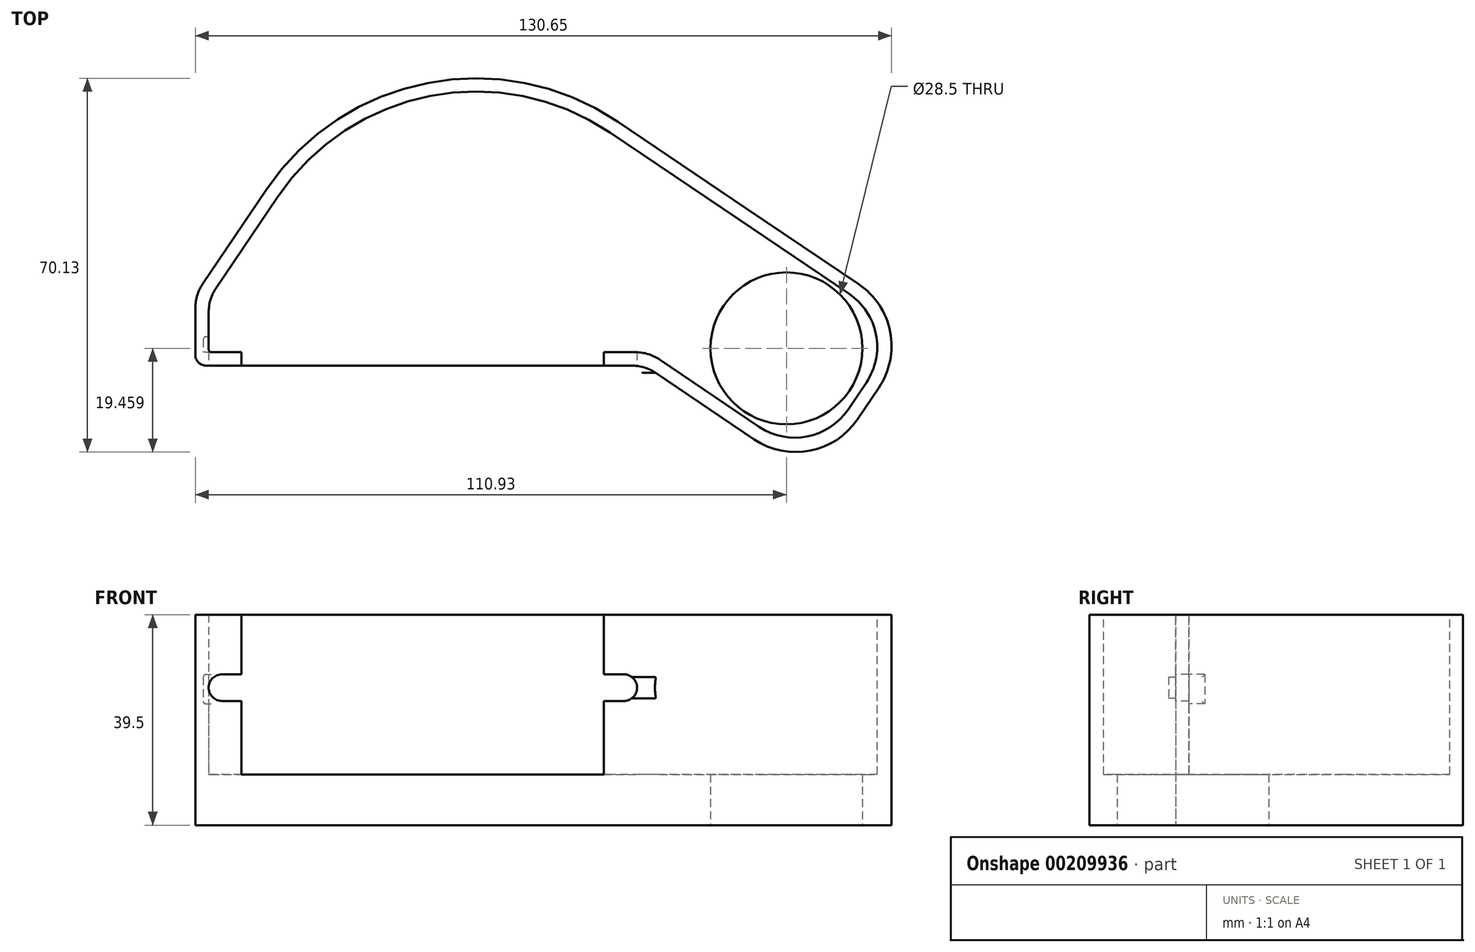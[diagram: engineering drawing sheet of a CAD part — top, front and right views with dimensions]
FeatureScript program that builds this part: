
annotation { "Feature Type Name" : "Feature", "Feature Type Description" : "" }
export const myFeature = defineFeature(function(context is Context, id is Id, definition is map)
    precondition{}
    {
        {
            var Q0;
            Q0=qCreatedBy(makeId("Top.planeOp"),FACE);
            var sketch = newSketch(context, id + "F0", { "sketchPlane" : qUnion([Q0])});
            skLineSegment(sketch, "E0", {"start": v(-46.29, -24.6) * mm, "end": v(36.31, -24.6) * mm});
            skLineSegment(sketch, "E1", {"start": v(-46.29, -24.6) * mm, "end": v(-46.29, -14.6) * mm});
            skLineSegment(sketch, "E2", {"start": v(36.31, -24.6) * mm, "end": v(53.15, 0.36) * mm});
            skLineSegment(sketch, "E3", {"start": v(53.15, 0.36) * mm, "end": v(-8.26, 41.78) * mm});
            skLineSegment(sketch, "E4", {"start": v(-8.26, 41.78) * mm, "end": v(-46.29, -14.6) * mm});
            skLineSegment(sketch, "E5", {"start": v(36.31, -24.6) * mm, "end": v(66.99, -45.29) * mm});
            skLineSegment(sketch, "E6", {"start": v(66.99, -45.29) * mm, "end": v(83.82, -20.33) * mm});
            skLineSegment(sketch, "E7", {"start": v(83.82, -20.33) * mm, "end": v(53.15, 0.36) * mm});
            skCircle(sketch, "E8", {"center": v(62.14, -23.86) * mm, "radius": 14.25 * mm});
            skSolve(sketch);
        }
        {
            var Q0;
            Q0 = qSketchRegion(id + "F0", true);
            extrude(context, id + "F1", {"entities" : qUnion([Q0]), "depth" : 9.15 * mm});
        }
        {
            var Q0;
            Q0=makeQuery(id+"F1.opExtrude","CAP_FACE",FACE,{"disambiguationData":[OSD([sQuery(id+"F0.wireOp",EDGE,"E0"),sQuery(id+"F0.wireOp",EDGE,"E1"),sQuery(id+"F0.wireOp",EDGE,"E2"),sQuery(id+"F0.wireOp",EDGE,"E3"),sQuery(id+"F0.wireOp",EDGE,"E4")])],"isStart":false});
            extrude(context, id + "F2", {"entities" : qUnion([Q0]), "operationType" : NewBodyOperationType.ADD, "depth" : 27.85 * mm});
        }
        {
            var Q0;
            Q0=makeQuery(id+"F2.opExtrude","CAP_FACE",FACE,{"disambiguationData":[OSD([sQuery(id+"F0.wireOp",EDGE,"E0"),sQuery(id+"F0.wireOp",EDGE,"E1"),sQuery(id+"F0.wireOp",EDGE,"E2"),sQuery(id+"F0.wireOp",EDGE,"E3"),sQuery(id+"F0.wireOp",EDGE,"E4")])],"isStart":false});
            var Q1;
            {var subQ0=sQuery(id+"F0.wireOp",EDGE,"E8");Q1=makeQuery(id+"F2.boolean.opBoolean","MERGE",FACE,{"derivedFrom":[makeQuery(id+"F1.opExtrude","SWEPT_FACE",FACE,{"disambiguationData":[OSD([subQ0])]}),makeQuery(id+"F2.opExtrude","SWEPT_FACE",FACE,{"disambiguationData":[OSD([subQ0])]})]});}
            shell(context, id + "F3", {"entities" : qUnion([Q0, Q1]), "thickness" : 2.5 * mm, "oppositeDirection" : true});
        }
        {
            var Q0;
            Q0=makeQuery(id+"F3.opShell","OFFSET_EDGE",EDGE,{"disambiguationData":[OSD([sQuery(id+"F0.wireOp",EDGE,"E3"),sQuery(id+"F0.wireOp",EDGE,"E4")])]});
            fillet(context, id + "F4", {"entities" : qUnion([Q0]), "radius" : 45 * mm, "tangentPropagation" : true, "allowEdgeOverflow" : false});
        }
        {
            var Q0;
            {var subQ0=sQuery(id+"F0.wireOp",EDGE,"E0");var subQ1=makeQuery(id+"F2.boolean.opBoolean","MERGE",FACE,{"derivedFrom":[makeQuery(id+"F1.opExtrude","SWEPT_FACE",FACE,{"disambiguationData":[OSD([subQ0])]}),makeQuery(id+"F2.opExtrude","SWEPT_FACE",FACE,{"disambiguationData":[OSD([subQ0])]})]});Q0=makeQuery(id+"FA12zDWdJS2ZKyh_1.boolean.opBoolean","MERGE",FACE,{"derivedFrom":[makeQuery(id+"FA8GY0G3jhh9Sxv_1.opShell","OFFSET_FACE",FACE,{"disambiguationData":[OSD([subQ0]),TDD([subQ1])]}),subQ1,makeQuery(id+"FA12zDWdJS2ZKyh_1.opExtrude","CAP_FACE",FACE,{"disambiguationData":[OSD([subQ0])],"isStart":false})]});}
            var sketch = newSketch(context, id + "F5", { "sketchPlane" : qUnion([Q0])});
            skCircle(sketch, "E9", {"center": v(-43.79, 23.3) * mm, "radius": 2.5 * mm});
            skCircle(sketch, "E10", {"center": v(31.61, 23.3) * mm, "radius": 2.5 * mm});
            skLineSegment(sketch, "E11", {"start": v(-43.79, 25.8) * mm, "end": v(-40.14, 25.8) * mm});
            skLineSegment(sketch, "E12", {"start": v(-43.79, 20.8) * mm, "end": v(-40.14, 20.8) * mm});
            skLineSegment(sketch, "E13", {"start": v(-40.14, 25.8) * mm, "end": v(-40.14, 37) * mm});
            skLineSegment(sketch, "E14", {"start": v(-40.14, 37) * mm, "end": v(27.86, 37) * mm});
            skLineSegment(sketch, "E15", {"start": v(-40.14, 20.8) * mm, "end": v(-40.14, 0) * mm});
            skLineSegment(sketch, "E16", {"start": v(27.86, 37) * mm, "end": v(27.86, 0) * mm});
            skPoint(sketch, "E16.endSnap0", {"position": v(27.86, 25.8) * mm});
            skLineSegment(sketch, "E17", {"start": v(-40.14, 0) * mm, "end": v(27.86, 0) * mm});
            skLineSegment(sketch, "E18", {"start": v(-40.14, 25.8) * mm, "end": v(-40.14, 20.8) * mm});
            skLineSegment(sketch, "E19", {"start": v(31.61, 25.8) * mm, "end": v(27.86, 25.8) * mm});
            skLineSegment(sketch, "E20", {"start": v(31.61, 20.8) * mm, "end": v(27.86, 20.8) * mm});
            skLineSegment(sketch, "E21", {"start": v(27.86, 20.8) * mm, "end": v(27.86, 25.8) * mm});
            skSolve(sketch);
        }
        {
            var Q0;
            Q0=makeQuery(id+"F5.imprint","IMPRINT",FACE,{"disambiguationData":[TD([[makeQuery(id+"F5.imprint","IMPRINT",EDGE,{"derivedFrom":sQuery(id+"F5.wireOp",EDGE,"E13")}),-1.0]])]});
            var Q1;
            {var subQ0=sQuery(id+"F5.wireOp",EDGE,"E19");Q1=makeQuery(id+"F5.imprint","IMPRINT",FACE,{"disambiguationData":[TD([[makeQuery(id+"F5.imprint","IMPRINT",EDGE,{"derivedFrom":subQ0}),1.0]])]});}
            var Q2;
            {var subQ0=sQuery(id+"F5.wireOp",EDGE,"E10");var subQ1=makeQuery(id+"F5.imprint","INTERSECT",VERTEX,{"derivedFrom":[subQ0,sQuery(id+"F5.wireOp",EDGE,"E19")]});Q2=makeQuery(id+"F5.imprint","IMPRINT",FACE,{"disambiguationData":[TD([[makeQuery(id+"F5.imprint","IMPRINT",EDGE,{"disambiguationData":[TD([[subQ1,-1.0]])],"derivedFrom":subQ0}),1.0]])]});}
            var Q3;
            {var subQ0=sQuery(id+"F5.wireOp",EDGE,"E11");Q3=makeQuery(id+"F5.imprint","IMPRINT",FACE,{"disambiguationData":[TD([[makeQuery(id+"F5.imprint","IMPRINT",EDGE,{"derivedFrom":subQ0}),-1.0]])]});}
            var Q4;
            {var subQ0=sQuery(id+"F5.wireOp",EDGE,"E9");var subQ1=makeQuery(id+"F5.imprint","INTERSECT",VERTEX,{"derivedFrom":[subQ0,sQuery(id+"F5.wireOp",EDGE,"E11")]});Q4=makeQuery(id+"F5.imprint","IMPRINT",FACE,{"disambiguationData":[TD([[makeQuery(id+"F5.imprint","IMPRINT",EDGE,{"disambiguationData":[TD([[subQ1,-1.0]])],"derivedFrom":subQ0}),1.0]])]});}
            var Q5;
            Q5=makeQuery(id+"F3.opShell","OFFSET_FACE",FACE,{"disambiguationData":[OSD([sQuery(id+"F0.wireOp",EDGE,"E0")])]});
            extrude(context, id + "F6", {"entities" : qUnion([Q0, Q1, Q2, Q3, Q4]), "operationType" : NewBodyOperationType.REMOVE, "oppositeDirection" : true, "endBoundEntityFace" : qUnion([Q5]), "depth" : 5 * mm});
        }
        {
            var Q0;
            {var subQ0=sQuery(id+"F0.wireOp",EDGE,"E4");var subQ1=sQuery(id+"F0.wireOp",EDGE,"E3");var subQ2=sQuery(id+"F0.wireOp",EDGE,"E2");var subQ3=sQuery(id+"F0.wireOp",EDGE,"E1");var subQ4=sQuery(id+"F0.wireOp",EDGE,"E0");Q0=makeQuery(id+"FDiYdYzYKmQPA4Z_1.boolean.opBoolean","MERGE",FACE,{"derivedFrom":[makeQuery(id+"FA12zDWdJS2ZKyh_1.boolean.opBoolean","MERGE",FACE,{"derivedFrom":[makeQuery(id+"F3.opShell","OFFSET_FACE",FACE,{"disambiguationData":[OSD([subQ4,subQ3,subQ2,subQ1,subQ0])]}),makeQuery(id+"FA12zDWdJS2ZKyh_1.opExtrude","SWEPT_FACE",FACE,{"disambiguationData":[OSD([subQ4])]})]}),makeQuery(id+"FDiYdYzYKmQPA4Z_1.opExtrude","CAP_FACE",FACE,{"disambiguationData":[OSD([subQ4,subQ3,subQ2,subQ1,subQ0])],"isStart":false})]});}
            extrude(context, id + "F7", {"entities" : qUnion([Q0]), "operationType" : NewBodyOperationType.ADD, "depth" : 7 * mm});
        }
        {
            var Q0;
            Q0=makeQuery(id+"F3.opShell","OFFSET_FACE",FACE,{"disambiguationData":[OSD([sQuery(id+"F0.wireOp",EDGE,"E1")])]});
            var sketch = newSketch(context, id + "F8", { "sketchPlane" : qUnion([Q0])});
            skLineSegment(sketch, "E22.bottom", {"start": v(-21.66, 25.78) * mm, "end": v(-24.6, 25.78) * mm});
            skLineSegment(sketch, "E22.top", {"start": v(-21.66, 20.24) * mm, "end": v(-24.6, 20.24) * mm});
            skLineSegment(sketch, "E22.left", {"start": v(-21.66, 25.78) * mm, "end": v(-21.66, 20.24) * mm});
            skLineSegment(sketch, "E22.right", {"start": v(-24.6, 25.78) * mm, "end": v(-24.6, 20.24) * mm});
            skSolve(sketch);
        }
        {
            var Q0;
            {var subQ2=sQuery(id+"F8.wireOp",EDGE,"E22.bottom");Q0=makeQuery(id+"F8.imprint","IMPRINT",FACE,{"disambiguationData":[TD([[makeQuery(id+"F8.imprint","IMPRINT",EDGE,{"derivedFrom":subQ2}),1.0]])]});}
            extrude(context, id + "F9", {"entities" : qUnion([Q0]), "operationType" : NewBodyOperationType.REMOVE, "oppositeDirection" : true, "depth" : 1 * mm});
        }
        {
            var Q0;
            Q0=makeQuery(id+"F9.boolean.opBoolean","COPY",EDGE,{"derivedFrom":makeQuery(id+"F9.opExtrude","CAP_EDGE",EDGE,{"disambiguationData":[OSD([sQuery(id+"F8.wireOp",EDGE,"E22.top")])],"isStart":true})});
            var Q1;
            Q1=makeQuery(id+"F9.boolean.opBoolean","COPY",EDGE,{"derivedFrom":makeQuery(id+"F9.opExtrude","CAP_EDGE",EDGE,{"disambiguationData":[OSD([sQuery(id+"F8.wireOp",EDGE,"E22.top")])],"isStart":false})});
            var Q2;
            Q2=makeQuery(id+"F9.boolean.opBoolean","COPY",EDGE,{"derivedFrom":makeQuery(id+"F9.opExtrude","CAP_EDGE",EDGE,{"disambiguationData":[OSD([sQuery(id+"F8.wireOp",EDGE,"E22.bottom")])],"isStart":true})});
            var Q3;
            Q3=makeQuery(id+"F9.boolean.opBoolean","COPY",EDGE,{"derivedFrom":makeQuery(id+"F9.opExtrude","CAP_EDGE",EDGE,{"disambiguationData":[OSD([sQuery(id+"F8.wireOp",EDGE,"E22.bottom")])],"isStart":false})});
            var Q4;
            Q4=makeQuery(id+"F9.boolean.opBoolean","COPY",EDGE,{"derivedFrom":makeQuery(id+"F9.opExtrude","CAP_EDGE",EDGE,{"disambiguationData":[OSD([sQuery(id+"F8.wireOp",EDGE,"E22.left")])],"isStart":false})});
            var Q5;
            Q5=makeQuery(id+"F9.boolean.opBoolean","COPY",EDGE,{"derivedFrom":makeQuery(id+"F9.opExtrude","CAP_EDGE",EDGE,{"disambiguationData":[OSD([sQuery(id+"F8.wireOp",EDGE,"E22.left")])],"isStart":true})});
            var Q6;
            {var subQ0=sQuery(id+"F0.wireOp",EDGE,"E1");var subQ1=sQuery(id+"F0.wireOp",EDGE,"E0");Q6=makeQuery(id+"F6.boolean.opBoolean","SPLIT",EDGE,{"disambiguationData":[TD([makeQuery(id+"F2.opExtrude","CAP_FACE",FACE,{"disambiguationData":[OSD([subQ1,subQ0,sQuery(id+"F0.wireOp",EDGE,"E3"),sQuery(id+"F0.wireOp",EDGE,"E4"),sQuery(id+"F0.wireOp",EDGE,"E5"),sQuery(id+"F0.wireOp",EDGE,"E6"),sQuery(id+"F0.wireOp",EDGE,"E7"),sQuery(id+"F0.wireOp",EDGE,"E8")])],"isStart":false})])],"derivedFrom":makeQuery(id+"F3.opShell","OFFSET_EDGE",EDGE,{"disambiguationData":[OSD([subQ1,subQ0])]})});}
            var Q7;
            {var subQ0=sQuery(id+"F0.wireOp",EDGE,"E1");var subQ1=sQuery(id+"F0.wireOp",EDGE,"E0");Q7=makeQuery(id+"F6.boolean.opBoolean","SPLIT",EDGE,{"disambiguationData":[TD([makeQuery(id+"F6.opExtrude","SWEPT_FACE",FACE,{"disambiguationData":[OSD([sQuery(id+"F5.wireOp",EDGE,"E17")])]})])],"derivedFrom":makeQuery(id+"F3.opShell","OFFSET_EDGE",EDGE,{"disambiguationData":[OSD([subQ1,subQ0])]})});}
            fillet(context, id + "F10", {"entities" : qUnion([Q0, Q1, Q2, Q3, Q4, Q5, Q6, Q7]), "radius" : .5 * mm, "tangentPropagation" : true, "allowEdgeOverflow" : false});
        }
        {
            var Q0;
            {var subQ0=sQuery(id+"F0.wireOp",EDGE,"E4");var subQ1=sQuery(id+"F0.wireOp",EDGE,"E1");Q0=makeQuery(id+"F2.boolean.opBoolean","MERGE",EDGE,{"derivedFrom":[makeQuery(id+"F1.opExtrude","SWEPT_EDGE",EDGE,{"disambiguationData":[OSD([subQ1,subQ0])]}),makeQuery(id+"F2.opExtrude","SWEPT_EDGE",EDGE,{"disambiguationData":[OSD([subQ1,subQ0])]})]});}
            var Q1;
            Q1=makeQuery(id+"F3.opShell","OFFSET_EDGE",EDGE,{"disambiguationData":[OSD([sQuery(id+"F0.wireOp",EDGE,"E1"),sQuery(id+"F0.wireOp",EDGE,"E4")])]});
            var Q2;
            Q2=makeQuery(id+"F3.opShell","OFFSET_EDGE",EDGE,{"disambiguationData":[OSD([sQuery(id+"F0.wireOp",EDGE,"E0"),sQuery(id+"F0.wireOp",EDGE,"E2"),sQuery(id+"F0.wireOp",EDGE,"E5")])]});
            var Q3;
            {var subQ0=sQuery(id+"F0.wireOp",EDGE,"E5");var subQ1=sQuery(id+"F0.wireOp",EDGE,"E2");var subQ2=sQuery(id+"F0.wireOp",EDGE,"E0");Q3=makeQuery(id+"F2.boolean.opBoolean","MERGE",EDGE,{"derivedFrom":[makeQuery(id+"F1.opExtrude","SWEPT_EDGE",EDGE,{"disambiguationData":[OSD([subQ2,subQ1,subQ0])]}),makeQuery(id+"F2.opExtrude","SWEPT_EDGE",EDGE,{"disambiguationData":[OSD([subQ2,subQ1,subQ0])]})]});}
            fillet(context, id + "F11", {"entities" : qUnion([Q0, Q1, Q2, Q3]), "radius" : 8 * mm, "tangentPropagation" : true, "allowEdgeOverflow" : false});
        }
        {
            var Q0;
            {var subQ0=sQuery(id+"F0.wireOp",EDGE,"E1");var subQ1=sQuery(id+"F0.wireOp",EDGE,"E0");Q0=makeQuery(id+"F2.boolean.opBoolean","MERGE",EDGE,{"derivedFrom":[makeQuery(id+"F1.opExtrude","SWEPT_EDGE",EDGE,{"disambiguationData":[OSD([subQ1,subQ0])]}),makeQuery(id+"F2.opExtrude","SWEPT_EDGE",EDGE,{"disambiguationData":[OSD([subQ1,subQ0])]})]});}
            fillet(context, id + "F12", {"entities" : qUnion([Q0]), "radius" : 2 * mm, "tangentPropagation" : true, "allowEdgeOverflow" : false});
        }
        {
            var Q0;
            Q0=makeQuery(id+"F3.opShell","OFFSET_EDGE",EDGE,{"disambiguationData":[OSD([sQuery(id+"F0.wireOp",EDGE,"E6"),sQuery(id+"F0.wireOp",EDGE,"E7")])]});
            var Q1;
            Q1=makeQuery(id+"F3.opShell","OFFSET_EDGE",EDGE,{"disambiguationData":[OSD([sQuery(id+"F0.wireOp",EDGE,"E5"),sQuery(id+"F0.wireOp",EDGE,"E6")])]});
            fillet(context, id + "F13", {"entities" : qUnion([Q0, Q1]), "radius" : 12 * mm, "tangentPropagation" : true, "allowEdgeOverflow" : false});
        }
        {
            var Q0;
            {var subQ0=sQuery(id+"F0.wireOp",EDGE,"E4");var subQ1=sQuery(id+"F0.wireOp",EDGE,"E3");Q0=makeQuery(id+"F2.boolean.opBoolean","MERGE",EDGE,{"derivedFrom":[makeQuery(id+"F1.opExtrude","SWEPT_EDGE",EDGE,{"disambiguationData":[OSD([subQ1,subQ0])]}),makeQuery(id+"F2.opExtrude","SWEPT_EDGE",EDGE,{"disambiguationData":[OSD([subQ1,subQ0])]})]});}
            fillet(context, id + "F14", {"entities" : qUnion([Q0]), "radius" : 47.5 * mm, "tangentPropagation" : true, "allowEdgeOverflow" : false});
        }
        {
            var Q0;
            {var subQ0=sQuery(id+"F0.wireOp",EDGE,"E6");var subQ1=sQuery(id+"F0.wireOp",EDGE,"E5");Q0=makeQuery(id+"F2.boolean.opBoolean","MERGE",EDGE,{"derivedFrom":[makeQuery(id+"F1.opExtrude","SWEPT_EDGE",EDGE,{"disambiguationData":[OSD([subQ1,subQ0])]}),makeQuery(id+"F2.opExtrude","SWEPT_EDGE",EDGE,{"disambiguationData":[OSD([subQ1,subQ0])]})]});}
            var Q1;
            {var subQ0=sQuery(id+"F0.wireOp",EDGE,"E7");var subQ1=sQuery(id+"F0.wireOp",EDGE,"E6");Q1=makeQuery(id+"F2.boolean.opBoolean","MERGE",EDGE,{"derivedFrom":[makeQuery(id+"F1.opExtrude","SWEPT_EDGE",EDGE,{"disambiguationData":[OSD([subQ1,subQ0])]}),makeQuery(id+"F2.opExtrude","SWEPT_EDGE",EDGE,{"disambiguationData":[OSD([subQ1,subQ0])]})]});}
            fillet(context, id + "F15", {"entities" : qUnion([Q0, Q1]), "radius" : 14 * mm, "tangentPropagation" : true, "allowEdgeOverflow" : false});
        }
    });
